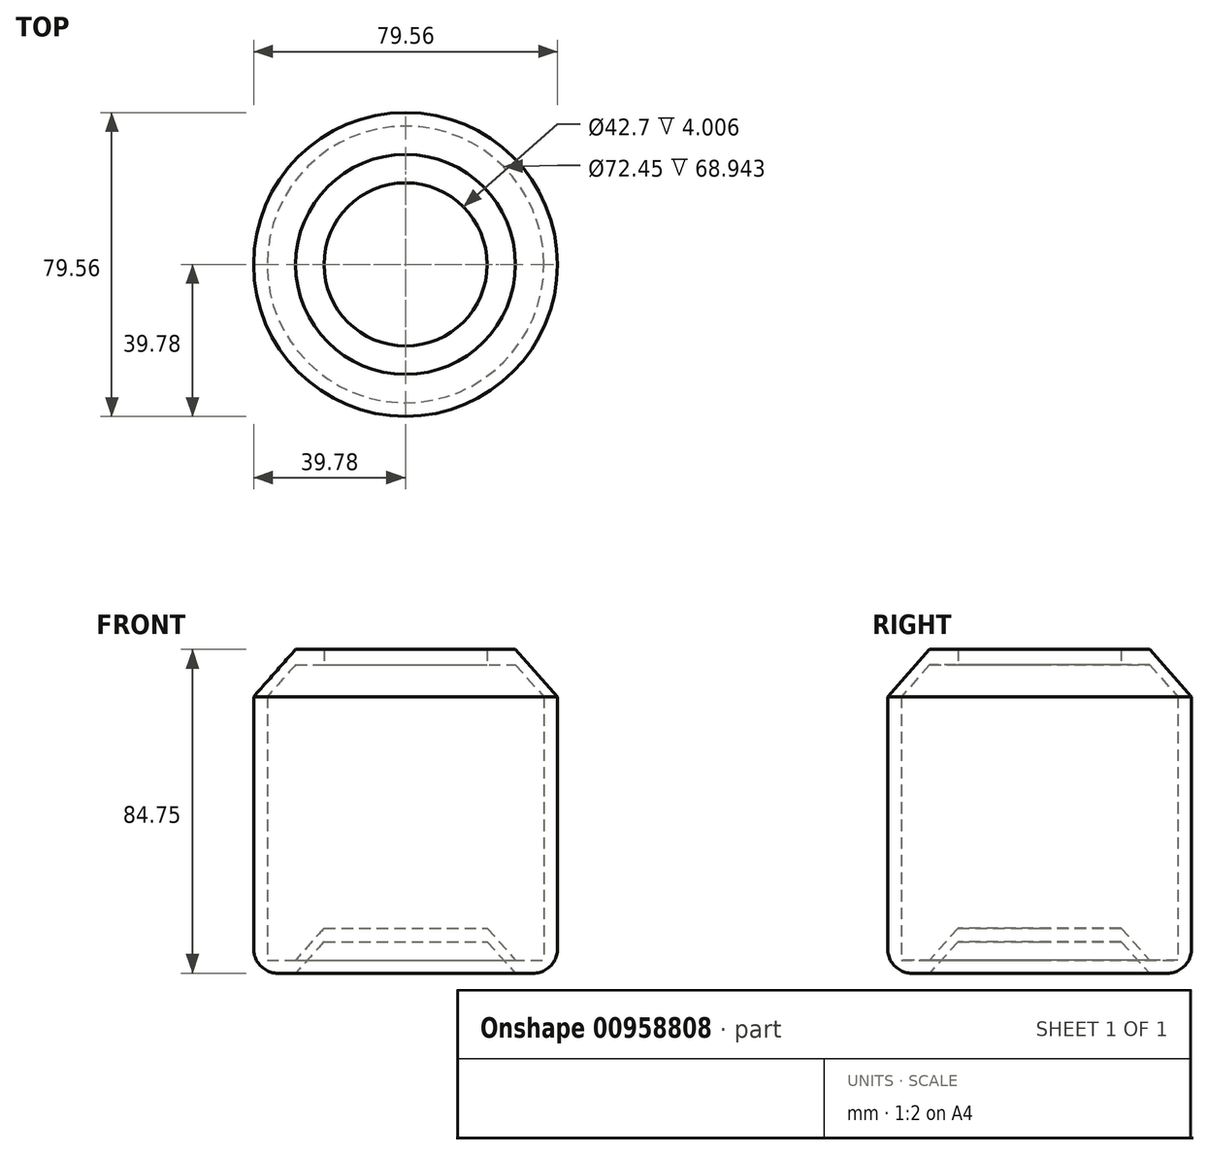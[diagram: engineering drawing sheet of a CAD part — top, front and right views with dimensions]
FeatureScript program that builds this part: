
annotation { "Feature Type Name" : "Feature", "Feature Type Description" : "" }
export const myFeature = defineFeature(function(context is Context, id is Id, definition is map)
    precondition{}
    {
        {
            var Q0;
            Q0=qCreatedBy(makeId("Front.planeOp"),FACE);
            var sketch = newSketch(context, id + "F0", { "sketchPlane" : qUnion([Q0])});
            skLineSegment(sketch, "E0", {"start": v(0, 0) * mm, "end": v(0, 68.37) * mm, "construction": true});
            skLineSegment(sketch, "E1", {"start": v(0, 0) * mm, "end": v(21.35, 0) * mm});
            skLineSegment(sketch, "E2", {"start": v(21.35, 0) * mm, "end": v(28.78, -8.25) * mm});
            skLineSegment(sketch, "E3", {"start": v(28.78, -8.25) * mm, "end": v(33.43, -8.25) * mm});
            skLineSegment(sketch, "E4", {"start": v(39.78, -1.9) * mm, "end": v(39.78, 64.1) * mm});
            skLineSegment(sketch, "E5", {"start": v(39.78, 64.1) * mm, "end": v(28.78, 76.5) * mm});
            skLineSegment(sketch, "E6", {"start": v(28.78, 76.5) * mm, "end": v(21.35, 76.5) * mm});
            skLineSegment(sketch, "E7", {"start": v(21.35, 76.5) * mm, "end": v(21.35, 72.5) * mm});
            skLineSegment(sketch, "E8", {"start": v(21.35, 72.5) * mm, "end": v(28.78, 72.5) * mm});
            skLineSegment(sketch, "E9", {"start": v(28.78, 72.5) * mm, "end": v(36.22, 64.1) * mm});
            skLineSegment(sketch, "E10", {"start": v(36.22, 64.1) * mm, "end": v(36.22, -4.84) * mm});
            skLineSegment(sketch, "E11", {"start": v(36.22, -4.84) * mm, "end": v(28.78, -4.84) * mm});
            skLineSegment(sketch, "E12", {"start": v(28.78, -4.84) * mm, "end": v(24.5, 0) * mm});
            skLineSegment(sketch, "E13", {"start": v(24.5, 0) * mm, "end": v(21.35, 3.54) * mm});
            skLineSegment(sketch, "E14", {"start": v(21.35, 3.54) * mm, "end": v(0, 3.54) * mm});
            skLineSegment(sketch, "E15", {"start": v(0, 3.54) * mm, "end": v(0, 0) * mm});
            skPoint(sketch, "E16.visualSharp", {"position": v(39.78, -8.25) * mm});
            skArc(sketch, "E16.filletArc", {"start": v(33.43, -8.25) * mm, "mid": v(37.92, -6.4) * mm, "end": v(39.78, -1.9) * mm});
            skSolve(sketch);
        }
        {
            var Q0;
            Q0=makeQuery(id+"F0.imprint","IMPRINT",FACE,{"disambiguationData":[TD([[makeQuery(id+"F0.imprint","IMPRINT",EDGE,{"derivedFrom":sQuery(id+"F0.wireOp",EDGE,"E1")}),1.0]])]});
            var Q1;
            Q1=sQuery(id+"F0.wireOp",EDGE,"E0");
            revolve(context, id + "F1", {"surfaceOperationType" : NewSurfaceOperationType.NEW, "entities" : qUnion([Q0]), "axis" : qUnion([Q1]), "revolveType" : RevolveType.FULL});
        }
    });
